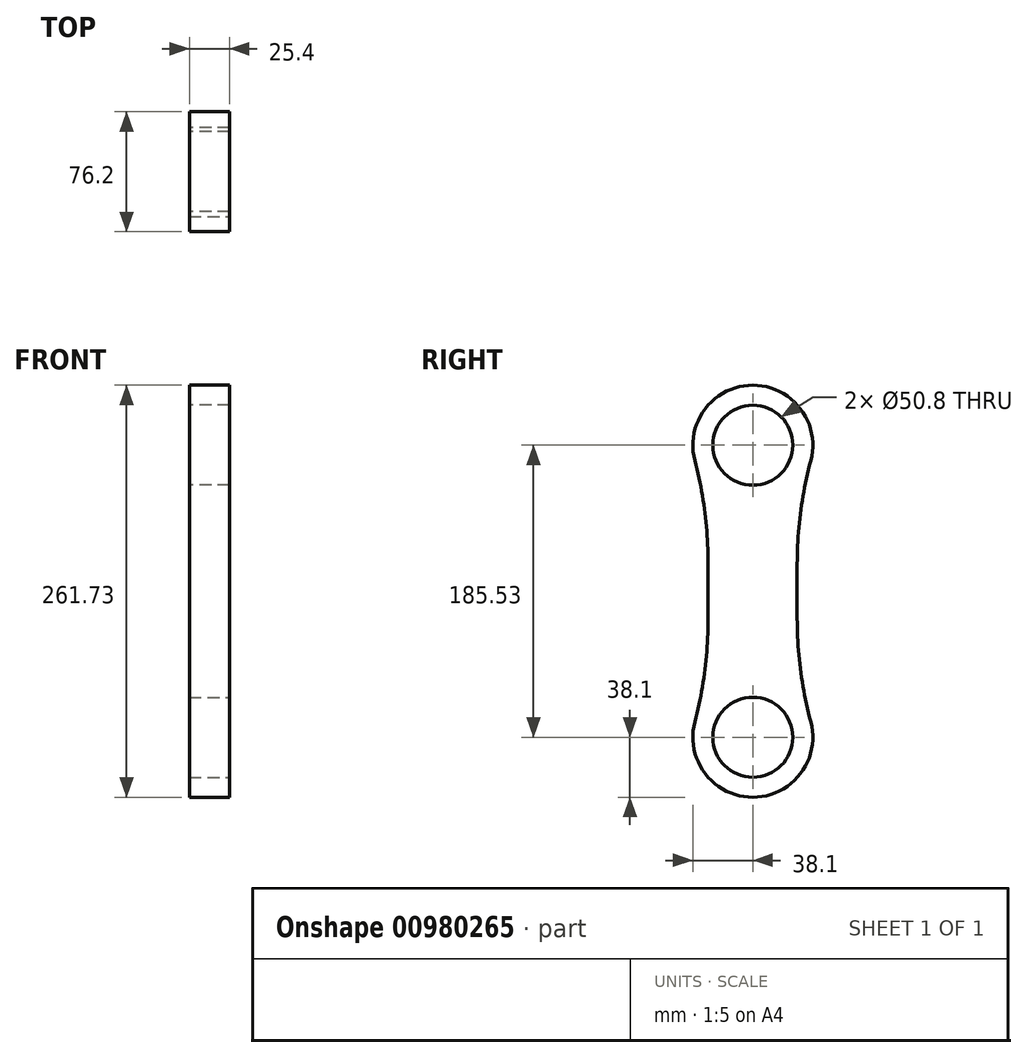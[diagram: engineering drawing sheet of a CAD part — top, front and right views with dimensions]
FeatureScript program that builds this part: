
annotation { "Feature Type Name" : "Feature", "Feature Type Description" : "" }
export const myFeature = defineFeature(function(context is Context, id is Id, definition is map)
    precondition{}
    {
        {
            var Q0;
            Q0=qCreatedBy(makeId("Right.planeOp"),FACE);
            var sketch = newSketch(context, id + "F0", { "sketchPlane" : qUnion([Q0])});
            skCircle(sketch, "E0", {"center": v(0, 0) * mm, "radius": 38.1 * mm});
            skSolve(sketch);
        }
        {
            var Q0;
            Q0=qCreatedBy(makeId("Right.planeOp"),FACE);
            var sketch = newSketch(context, id + "F1", { "sketchPlane" : qUnion([Q0])});
            skCircle(sketch, "E1", {"center": v(0, -185.53) * mm, "radius": 38.1 * mm});
            skSolve(sketch);
        }
        {
            var Q0;
            Q0=qCreatedBy(makeId("Right.planeOp"),FACE);
            var sketch = newSketch(context, id + "F2", { "sketchPlane" : qUnion([Q0])});
            skLineSegment(sketch, "E2.bottom", {"start": v(-28.45, -24.55) * mm, "end": v(28.18, -24.55) * mm});
            skLineSegment(sketch, "E2.top", {"start": v(-28.45, -160.85) * mm, "end": v(28.18, -160.85) * mm});
            skLineSegment(sketch, "E2.left", {"start": v(-28.45, -24.55) * mm, "end": v(-28.45, -160.85) * mm});
            skLineSegment(sketch, "E2.right", {"start": v(28.18, -24.55) * mm, "end": v(28.18, -160.85) * mm});
            skSolve(sketch);
        }
        {
            var Q0;
            Q0=makeQuery(id+"F2.imprint","IMPRINT",FACE,{"disambiguationData":[TD([[makeQuery(id+"F2.imprint","IMPRINT",EDGE,{"derivedFrom":sQuery(id+"F2.wireOp",EDGE,"E2.bottom")}),-1.0]])]});
            extrude(context, id + "F3", {"entities" : qUnion([Q0]), "depth" : 25.4 * mm, "offsetDistance" : 25.4 * mm});
        }
        {
            var Q0;
            Q0=makeQuery(id+"F0.imprint","IMPRINT",FACE,{"disambiguationData":[TD([[makeQuery(id+"F0.imprint","IMPRINT",EDGE,{"derivedFrom":sQuery(id+"F0.wireOp",EDGE,"E0")}),1.0]])]});
            extrude(context, id + "F4", {"entities" : qUnion([Q0]), "operationType" : NewBodyOperationType.ADD, "depth" : 25.4 * mm, "offsetDistance" : 25.4 * mm});
        }
        {
            var Q0;
            Q0=makeQuery(id+"F1.imprint","IMPRINT",FACE,{"disambiguationData":[TD([[makeQuery(id+"F1.imprint","IMPRINT",EDGE,{"derivedFrom":sQuery(id+"F1.wireOp",EDGE,"E1")}),1.0]])]});
            extrude(context, id + "F5", {"entities" : qUnion([Q0]), "operationType" : NewBodyOperationType.ADD, "depth" : 25.4 * mm, "offsetDistance" : 25.4 * mm});
        }
        {
            var Q0;
            Q0=sQuery(id+"F0.wireOp",VERTEX,"E0.center");
            var Q1;
            Q1=makeQuery(id+"F3.opExtrude","SWEPT_BODY",BODY,{"disambiguationData":[OSD([sQuery(id+"F2.wireOp",EDGE,"E2.bottom"),sQuery(id+"F2.wireOp",EDGE,"E2.top"),sQuery(id+"F2.wireOp",EDGE,"E2.left"),sQuery(id+"F2.wireOp",EDGE,"E2.right")])]});
            hole(context, id + "F6", {"style" : HoleStyle.SIMPLE, "endStyle" : HoleEndStyle.THROUGH, "oppositeDirection" : true, "holeDiameter" : 50.8 * mm, "majorDiameter" : 6.35 * mm, "isTappedThrough" : true, "tappedDepth" : 12.7 * mm, "tapClearance" : 3, "locations" : qUnion([Q0]), "scope" : qUnion([Q1])});
        }
        {
            var Q0;
            Q0=makeQuery(id+"F5.boolean.opBoolean","MERGE",FACE,{"derivedFrom":[makeQuery(id+"F4.boolean.opBoolean","MERGE",FACE,{"derivedFrom":[makeQuery(id+"F3.opExtrude","CAP_FACE",FACE,{"disambiguationData":[OSD([sQuery(id+"F2.wireOp",EDGE,"E2.bottom"),sQuery(id+"F2.wireOp",EDGE,"E2.top"),sQuery(id+"F2.wireOp",EDGE,"E2.left"),sQuery(id+"F2.wireOp",EDGE,"E2.right")])],"isStart":false}),makeQuery(id+"F4.opExtrude","CAP_FACE",FACE,{"disambiguationData":[OSD([sQuery(id+"F0.wireOp",EDGE,"E0")])],"isStart":false})]}),makeQuery(id+"F5.opExtrude","CAP_FACE",FACE,{"disambiguationData":[OSD([sQuery(id+"F1.wireOp",EDGE,"E1")])],"isStart":false})]});
            var sketch = newSketch(context, id + "F7", { "sketchPlane" : qUnion([Q0])});
            skCircle(sketch, "E3", {"center": v(0, -185.53) * mm, "radius": 38.1 * mm});
            skSolve(sketch);
        }
        {
            var Q0;
            Q0=sQuery(id+"F7.wireOp",VERTEX,"E3.center");
            var Q1;
            Q1=makeQuery(id+"F3.opExtrude","SWEPT_BODY",BODY,{"disambiguationData":[OSD([sQuery(id+"F2.wireOp",EDGE,"E2.bottom"),sQuery(id+"F2.wireOp",EDGE,"E2.top"),sQuery(id+"F2.wireOp",EDGE,"E2.left"),sQuery(id+"F2.wireOp",EDGE,"E2.right")])]});
            hole(context, id + "F8", {"style" : HoleStyle.SIMPLE, "endStyle" : HoleEndStyle.THROUGH, "holeDiameter" : 50.8 * mm, "majorDiameter" : 6.35 * mm, "isTappedThrough" : true, "tappedDepth" : 12.7 * mm, "tapClearance" : 3, "locations" : qUnion([Q0]), "scope" : qUnion([Q1])});
        }
        {
            var Q0;
            Q0=makeQuery(id+"F5.boolean.opBoolean","MERGE",FACE,{"derivedFrom":[makeQuery(id+"F4.boolean.opBoolean","MERGE",FACE,{"derivedFrom":[makeQuery(id+"F3.opExtrude","CAP_FACE",FACE,{"disambiguationData":[OSD([sQuery(id+"F2.wireOp",EDGE,"E2.bottom"),sQuery(id+"F2.wireOp",EDGE,"E2.top"),sQuery(id+"F2.wireOp",EDGE,"E2.left"),sQuery(id+"F2.wireOp",EDGE,"E2.right")])],"isStart":false}),makeQuery(id+"F4.opExtrude","CAP_FACE",FACE,{"disambiguationData":[OSD([sQuery(id+"F0.wireOp",EDGE,"E0")])],"isStart":false})]}),makeQuery(id+"F5.opExtrude","CAP_FACE",FACE,{"disambiguationData":[OSD([sQuery(id+"F1.wireOp",EDGE,"E1")])],"isStart":false})]});
            var sketch = newSketch(context, id + "F9", { "sketchPlane" : qUnion([Q0])});
            skSolve(sketch);
        }
        {
            var Q0;
            {var subQ3=sQuery(id+"F2.wireOp",EDGE,"E2.right");Q0=makeQuery(id+"F9.imprint","IMPRINT",FACE,{"disambiguationData":[TD([[makeQuery(id+"F9.imprint","IMPRINT",EDGE,{"derivedFrom":makeQuery(id+"F3.opExtrude","CAP_EDGE",EDGE,{"disambiguationData":[OSD([subQ3])],"isStart":false})}),-1.0]])]});}
            var sketch = newSketch(context, id + "F10", { "sketchPlane" : qUnion([Q0])});
            skCircle(sketch, "E4", {"center": v(0, 0) * mm, "radius": 38.1 * mm});
            skSolve(sketch);
        }
        {
            var Q0;
            Q0=makeQuery(id+"F5.boolean.opBoolean","INTERSECT",EDGE,{"derivedFrom":[makeQuery(id+"F3.opExtrude","SWEPT_FACE",FACE,{"disambiguationData":[OSD([sQuery(id+"F2.wireOp",EDGE,"E2.left")])]}),makeQuery(id+"F5.opExtrude","SWEPT_FACE",FACE,{"disambiguationData":[OSD([sQuery(id+"F1.wireOp",EDGE,"E1")])]})]});
            var Q1;
            Q1=makeQuery(id+"F3.opExtrude","SWEPT_EDGE",EDGE,{"disambiguationData":[OSD([sQuery(id+"F2.wireOp",EDGE,"E2.top"),sQuery(id+"F2.wireOp",EDGE,"E2.right")])]});
            var Q2;
            Q2=makeQuery(id+"F4.boolean.opBoolean","INTERSECT",EDGE,{"derivedFrom":[makeQuery(id+"F3.opExtrude","SWEPT_FACE",FACE,{"disambiguationData":[OSD([sQuery(id+"F2.wireOp",EDGE,"E2.left")])]}),makeQuery(id+"F4.opExtrude","SWEPT_FACE",FACE,{"disambiguationData":[OSD([sQuery(id+"F0.wireOp",EDGE,"E0")])]})]});
            var Q3;
            Q3=makeQuery(id+"F4.boolean.opBoolean","INTERSECT",EDGE,{"derivedFrom":[makeQuery(id+"F3.opExtrude","SWEPT_FACE",FACE,{"disambiguationData":[OSD([sQuery(id+"F2.wireOp",EDGE,"E2.right")])]}),makeQuery(id+"F4.opExtrude","SWEPT_FACE",FACE,{"disambiguationData":[OSD([sQuery(id+"F0.wireOp",EDGE,"E0")])]})]});
            fillet(context, id + "F11", {"entities" : qUnion([Q0, Q1, Q2, Q3]), "radius" : 254 * mm, "tangentPropagation" : true, "rho" : 0.5, "crossSection" : FilletCrossSection.CONIC, "allowEdgeOverflow" : false});
        }
        {
            var Q0;
            Q0=makeQuery(id+"F5.boolean.opBoolean","INTERSECT",EDGE,{"derivedFrom":[makeQuery(id+"F3.opExtrude","SWEPT_FACE",FACE,{"disambiguationData":[OSD([sQuery(id+"F2.wireOp",EDGE,"E2.right")])]}),makeQuery(id+"F5.opExtrude","SWEPT_FACE",FACE,{"disambiguationData":[OSD([sQuery(id+"F1.wireOp",EDGE,"E1")])]})]});
            fillet(context, id + "F12", {"entities" : qUnion([Q0]), "radius" : 254 * mm, "tangentPropagation" : true, "rho" : 0.5, "crossSection" : FilletCrossSection.CONIC, "allowEdgeOverflow" : false});
        }
    });
